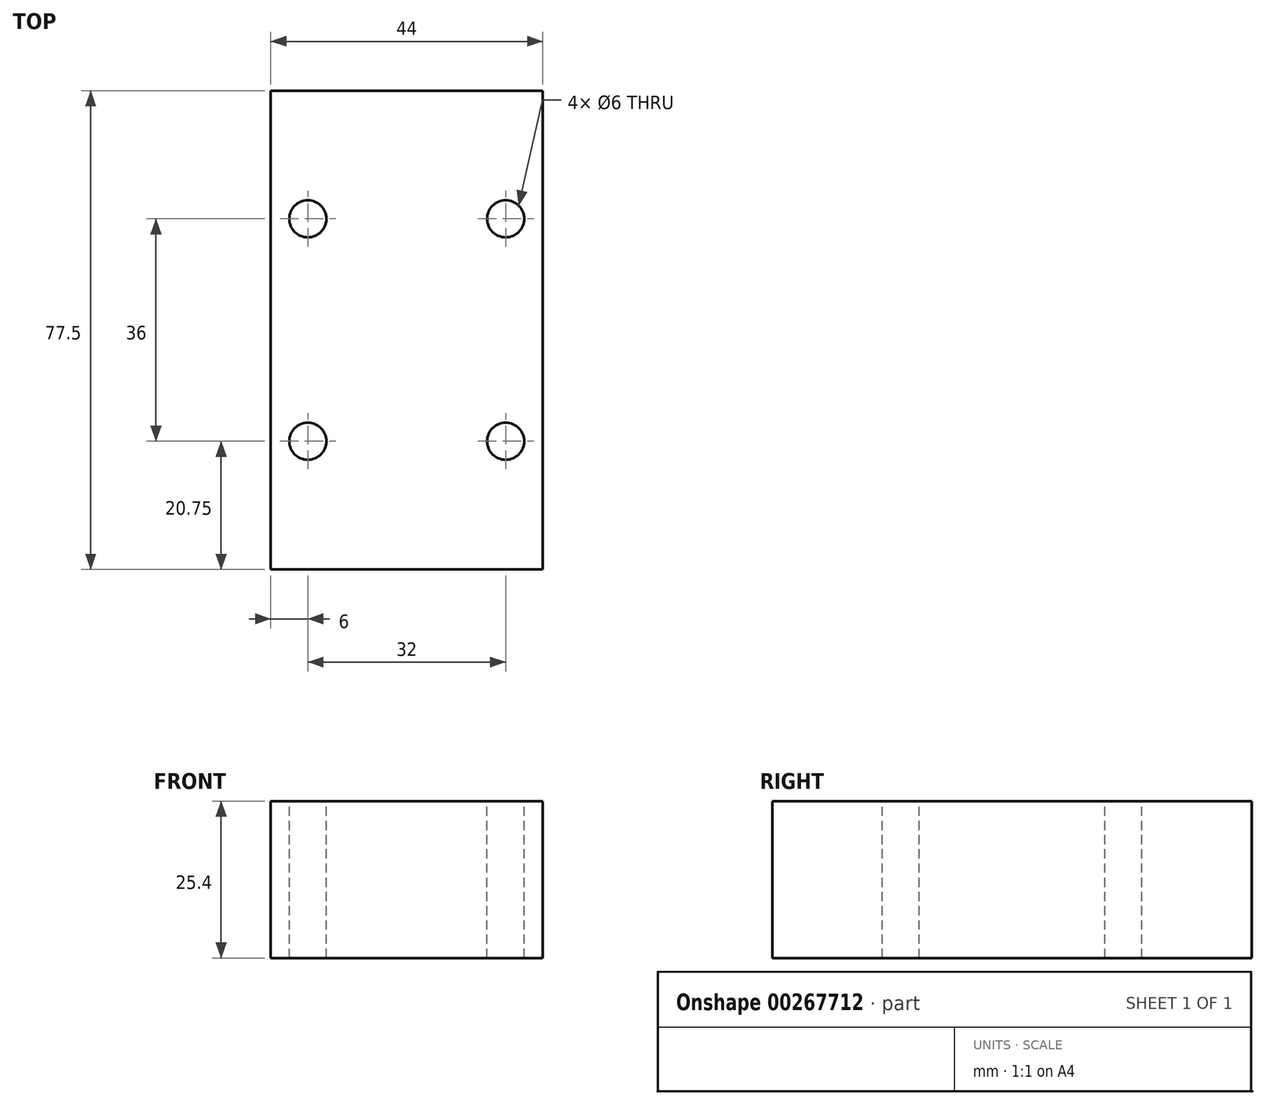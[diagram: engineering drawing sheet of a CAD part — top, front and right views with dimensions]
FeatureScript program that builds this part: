
annotation { "Feature Type Name" : "Feature", "Feature Type Description" : "" }
export const myFeature = defineFeature(function(context is Context, id is Id, definition is map)
    precondition{}
    {
        {
            var Q0;
            Q0=qCreatedBy(makeId("Front.planeOp"),FACE);
            var sketch = newSketch(context, id + "F0", { "sketchPlane" : qUnion([Q0])});
            skLineSegment(sketch, "E0.bottom", {"start": v(-22, 12.7) * mm, "end": v(22, 12.7) * mm});
            skLineSegment(sketch, "E0.top", {"start": v(-22, -12.7) * mm, "end": v(22, -12.7) * mm});
            skLineSegment(sketch, "E0.left", {"start": v(-22, 12.7) * mm, "end": v(-22, -12.7) * mm});
            skLineSegment(sketch, "E0.right", {"start": v(22, 12.7) * mm, "end": v(22, -12.7) * mm});
            skPoint(sketch, "E0.middle", {"position": v(0, 0) * mm});
            skSolve(sketch);
        }
        {
            var Q0;
            Q0=qSketchRegion(id+"F0",true);
            extrude(context, id + "F1", {"entities" : qUnion([Q0]), "oppositeDirection" : true, "depth" : 77.5 * mm});
        }
        {
            var Q0;
            Q0=makeQuery(id+"F1.opExtrude","SWEPT_FACE",FACE,{"disambiguationData":[OSD([sQuery(id+"F0.wireOp",EDGE,"E0.bottom")])]});
            var sketch = newSketch(context, id + "F2", { "sketchPlane" : qUnion([Q0])});
            skLineSegment(sketch, "E1.bottom", {"start": v(16, 118.22) * mm, "end": v(-16, 118.22) * mm, "construction": true});
            skLineSegment(sketch, "E1.top", {"start": v(16, -118.22) * mm, "end": v(-16, -118.22) * mm, "construction": true});
            skLineSegment(sketch, "E1.left", {"start": v(16, 118.22) * mm, "end": v(16, -118.22) * mm, "construction": true});
            skLineSegment(sketch, "E1.right", {"start": v(-16, 118.22) * mm, "end": v(-16, -118.22) * mm, "construction": true});
            skPoint(sketch, "E1.middle", {"position": v(0, 0) * mm});
            skLineSegment(sketch, "E2", {"start": v(-22, 38.75) * mm, "end": v(22, 38.75) * mm, "construction": true});
            skLineSegment(sketch, "E3.bottom", {"start": v(16, 56.75) * mm, "end": v(-25.34, 56.75) * mm, "construction": true});
            skLineSegment(sketch, "E3.top", {"start": v(16, 20.75) * mm, "end": v(-25.34, 20.75) * mm, "construction": true});
            skLineSegment(sketch, "E3.right", {"start": v(-25.34, 56.75) * mm, "end": v(-25.34, 20.75) * mm, "construction": true});
            skPoint(sketch, "E3.middle", {"position": v(-4.67, 38.75) * mm});
            skCircle(sketch, "E4", {"center": v(-16, 56.75) * mm, "radius": 3 * mm});
            skCircle(sketch, "E5", {"center": v(16, 56.75) * mm, "radius": 3 * mm});
            skCircle(sketch, "E6", {"center": v(-16, 20.75) * mm, "radius": 3 * mm});
            skCircle(sketch, "E7", {"center": v(16, 20.75) * mm, "radius": 3 * mm});
            skSolve(sketch);
        }
        {
            var Q0;
            Q0=makeQuery(id+"F2.imprint","IMPRINT",FACE,{"disambiguationData":[TD([[makeQuery(id+"F2.imprint","IMPRINT",EDGE,{"derivedFrom":sQuery(id+"F2.wireOp",EDGE,"E4")}),1.0]])]});
            var Q1;
            Q1=makeQuery(id+"F2.imprint","IMPRINT",FACE,{"disambiguationData":[TD([[makeQuery(id+"F2.imprint","IMPRINT",EDGE,{"derivedFrom":sQuery(id+"F2.wireOp",EDGE,"E6")}),1.0]])]});
            var Q2;
            Q2=makeQuery(id+"F2.imprint","IMPRINT",FACE,{"disambiguationData":[TD([[makeQuery(id+"F2.imprint","IMPRINT",EDGE,{"derivedFrom":sQuery(id+"F2.wireOp",EDGE,"E7")}),1.0]])]});
            var Q3;
            Q3=makeQuery(id+"F2.imprint","IMPRINT",FACE,{"disambiguationData":[TD([[makeQuery(id+"F2.imprint","IMPRINT",EDGE,{"derivedFrom":sQuery(id+"F2.wireOp",EDGE,"E5")}),1.0]])]});
            var Q4;
            Q4=sQuery(id+"F2.wireOp",EDGE,"E4");
            var Q5;
            Q5=sQuery(id+"F2.wireOp",EDGE,"E6");
            var Q6;
            Q6=sQuery(id+"F2.wireOp",EDGE,"E7");
            var Q7;
            Q7=sQuery(id+"F2.wireOp",EDGE,"E5");
            extrude(context, id + "F3", {"entities" : qUnion([Q0, Q1, Q2, Q3]), "operationType" : NewBodyOperationType.REMOVE, "surfaceEntities" : qUnion([Q4, Q5, Q6, Q7]), "endBound" : BoundingType.THROUGH_ALL, "oppositeDirection" : true, "depth" : 25 * mm});
        }
    });
